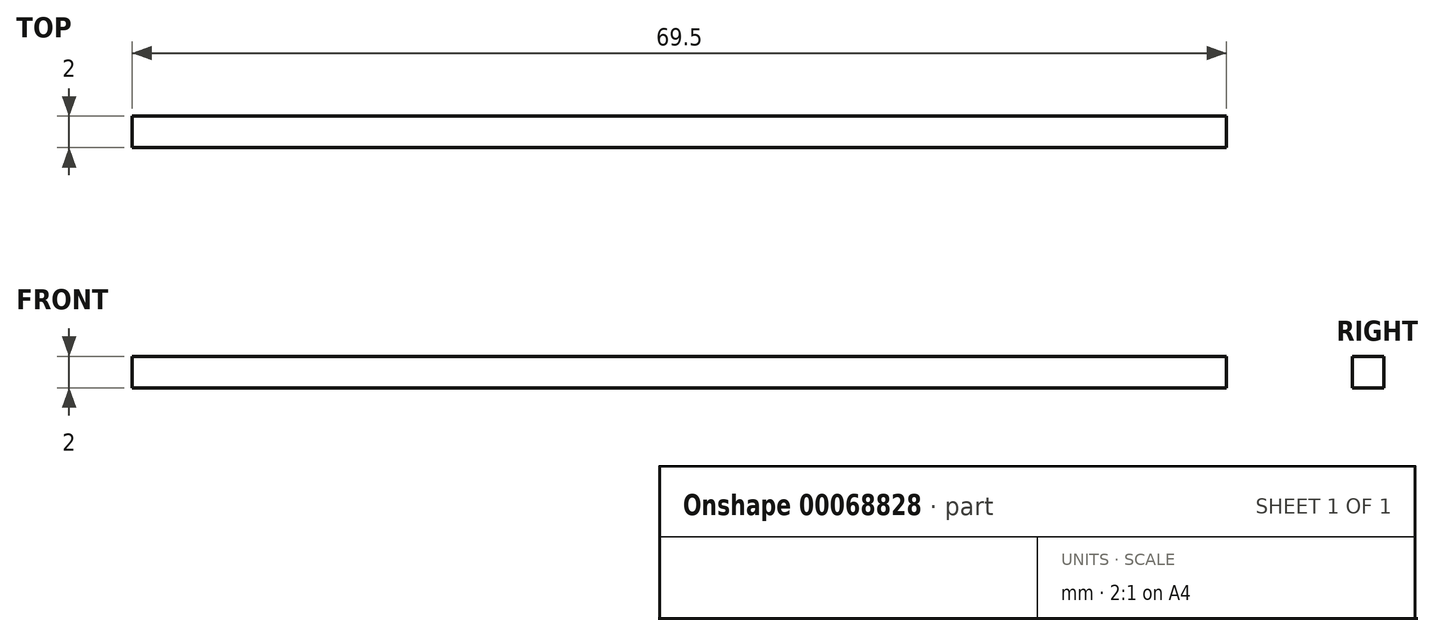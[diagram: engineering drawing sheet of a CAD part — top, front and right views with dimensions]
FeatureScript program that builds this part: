
annotation { "Feature Type Name" : "Feature", "Feature Type Description" : "" }
export const myFeature = defineFeature(function(context is Context, id is Id, definition is map)
    precondition{}
    {
        {
            var Q0;
            Q0=qCreatedBy(makeId("Top.planeOp"),FACE);
            var sketch = newSketch(context, id + "F0", { "sketchPlane" : qUnion([Q0])});
            skLineSegment(sketch, "E0.bottom", {"start": v(0, 0) * mm, "end": v(69.5, 0) * mm});
            skLineSegment(sketch, "E0.top", {"start": v(0, -2) * mm, "end": v(69.5, -2) * mm});
            skLineSegment(sketch, "E0.left", {"start": v(0, 0) * mm, "end": v(0, -2) * mm});
            skLineSegment(sketch, "E0.right", {"start": v(69.5, 0) * mm, "end": v(69.5, -2) * mm});
            skSolve(sketch);
        }
        {
            var Q0;
            Q0 = qSketchRegion(id + "F0", true);
            extrude(context, id + "F1", {"entities" : qUnion([Q0]), "depth" : 2 * mm});
        }
    });
